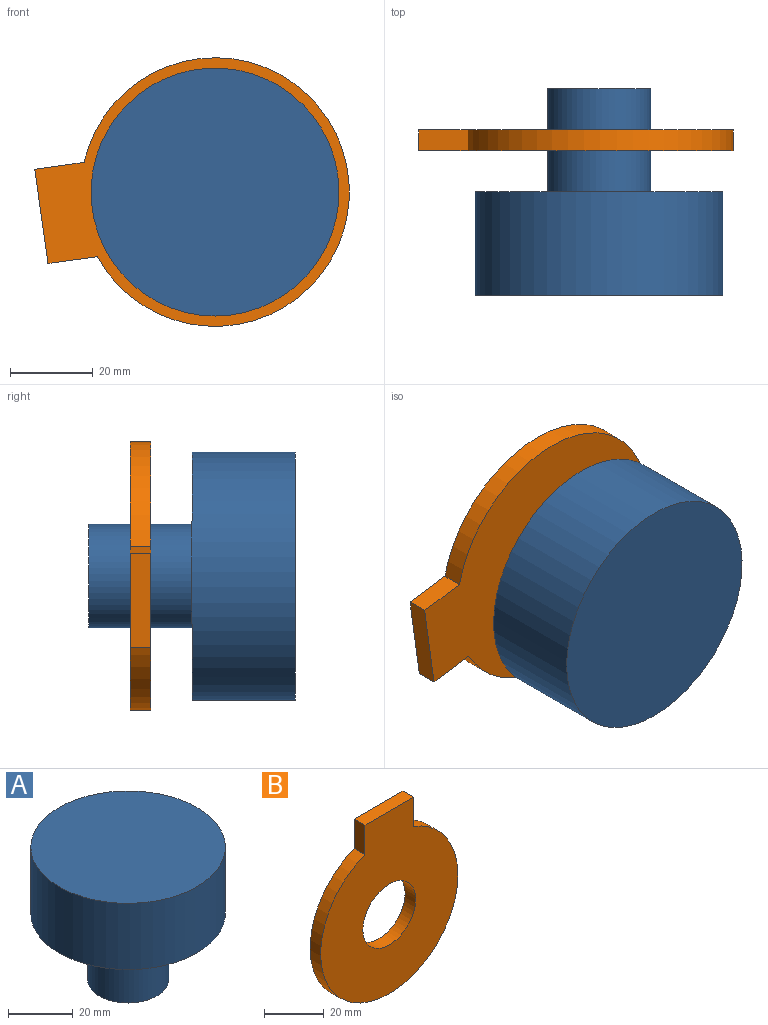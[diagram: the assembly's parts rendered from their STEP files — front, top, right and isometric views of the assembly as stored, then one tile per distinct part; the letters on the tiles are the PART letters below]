
ASSEMBLY  parts=2 mates=2
PART A: 5 faces, bbox 60x60x50 mm
  f0: cylinder r=12.5mm len=25mm, axis (0,0,-1), area 1963.5mm2, adj f1,f4
  f1: plane 25x25mm, normal (0,0,-1), area 490.9mm2, adj f0
  f2: cylinder r=30mm len=60mm, axis (0,0,-1), area 4712.4mm2, adj f3,f4
  f3: plane 60x60mm, normal (0,0,1), area 2827.4mm2, adj f2
  f4: plane 60x60mm, normal (0,0,-1), area 2336.6mm2, adj f0,f2
PART B: 7 faces, bbox 65x5x74.9 mm
  f0: plane 23.02x5mm, normal (0,0,1), area 115.1mm2, adj f1,f4,f5,f6
  f1: plane 12.04x5mm, normal (-1,0,0), area 60.2mm2, adj f0,f2,f5,f6
  f2: cylinder r=32.5mm len=65mm, axis (0,1,0), area 903.4mm2, adj f1,f4,f5,f6
  f3: cylinder r=12.5mm len=25mm, axis (0,1,0), area 392.7mm2, adj f5,f6
  f4: plane 12.04x5mm, normal (1,0,0), area 60.2mm2, adj f0,f2,f5,f6
  f5: plane 74.93x65mm, normal (0,-1,0), area 3072mm2, adj f0,f1,f2,f3,f4
  f6: plane 74.93x65mm, normal (0,1,0), area 3072mm2, adj f0,f1,f2,f3,f4
PLACE A rot(axis=(0.58,0.58,-0.58),120deg) t=(-13.63,-19.81,5.77)mm fixed
PLACE B rot(axis=(0,-1,0),98deg) t=(-13.63,-29.81,5.77)mm
MATE revolute B.f2 <-> A.f0  axis (0,1,0) through (-13.63,-32.31,5.77)mm
MATE parallel A.f0 <-> B.f2  axis (0,1,0) through (-13.63,-19.81,5.77)mm
